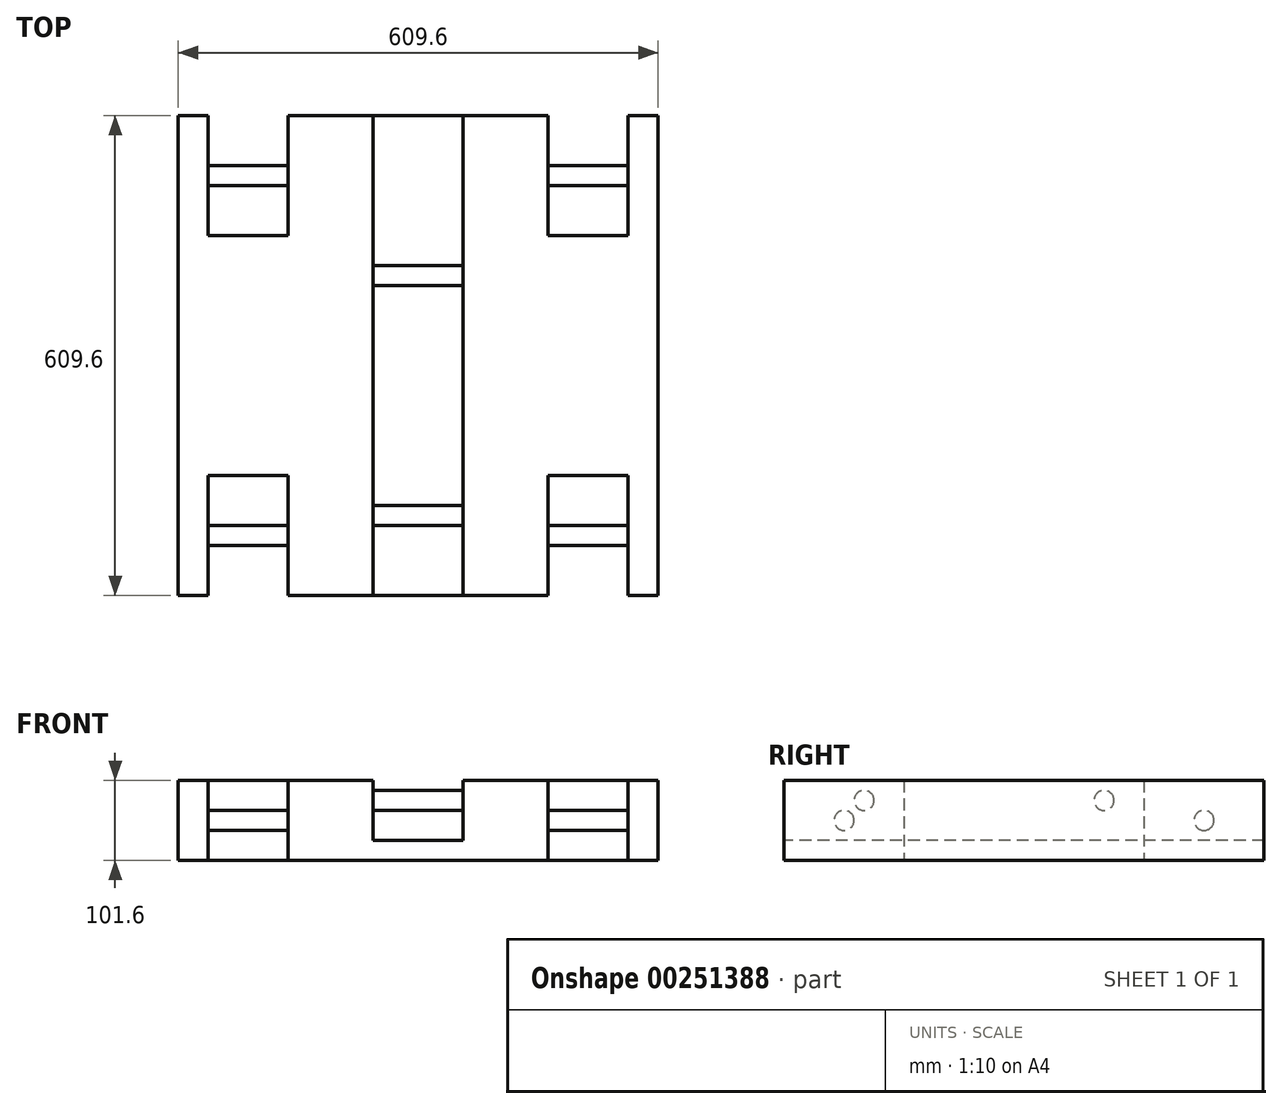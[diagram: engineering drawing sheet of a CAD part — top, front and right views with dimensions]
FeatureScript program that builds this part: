
annotation { "Feature Type Name" : "Feature", "Feature Type Description" : "" }
export const myFeature = defineFeature(function(context is Context, id is Id, definition is map)
    precondition{}
    {
        {
            var Q0;
            Q0=qCreatedBy(makeId("Top.planeOp"),FACE);
            var sketch = newSketch(context, id + "F0", { "sketchPlane" : qUnion([Q0])});
            skLineSegment(sketch, "E0.bottom", {"start": v(-126.74, -80.73) * mm, "end": v(482.86, -80.73) * mm});
            skLineSegment(sketch, "E0.top", {"start": v(-126.74, 528.87) * mm, "end": v(482.86, 528.87) * mm});
            skLineSegment(sketch, "E0.left", {"start": v(-126.74, -80.73) * mm, "end": v(-126.74, 528.87) * mm});
            skLineSegment(sketch, "E0.right", {"start": v(482.86, -80.73) * mm, "end": v(482.86, 528.87) * mm});
            skSolve(sketch);
        }
        {
            var Q0;
            Q0=makeQuery(id+"F0.imprint","IMPRINT",FACE,{"disambiguationData":[TD([[makeQuery(id+"F0.imprint","IMPRINT",EDGE,{"derivedFrom":sQuery(id+"F0.wireOp",EDGE,"E0.bottom")}),1.0]])]});
            extrude(context, id + "F1", {"entities" : qUnion([Q0]), "depth" : 101.6 * mm});
        }
        {
            var Q0;
            Q0=qCreatedBy(makeId("Top.planeOp"),FACE);
            var sketch = newSketch(context, id + "F2", { "sketchPlane" : qUnion([Q0])});
            skLineSegment(sketch, "E1.bottom", {"start": v(444.76, -80.73) * mm, "end": v(343.16, -80.73) * mm});
            skLineSegment(sketch, "E1.top", {"start": v(444.76, 71.67) * mm, "end": v(343.16, 71.67) * mm});
            skLineSegment(sketch, "E1.left", {"start": v(444.76, -80.73) * mm, "end": v(444.76, 71.67) * mm});
            skLineSegment(sketch, "E1.right", {"start": v(343.16, -80.73) * mm, "end": v(343.16, 71.67) * mm});
            skPoint(sketch, "E1.middle", {"position": v(393.96, 0) * mm});
            skLineSegment(sketch, "E2.bottom", {"start": v(12.96, -80.73) * mm, "end": v(-88.64, -80.73) * mm});
            skLineSegment(sketch, "E2.top", {"start": v(12.96, 71.67) * mm, "end": v(-88.64, 71.67) * mm});
            skLineSegment(sketch, "E2.left", {"start": v(12.96, -80.73) * mm, "end": v(12.96, 71.67) * mm});
            skLineSegment(sketch, "E2.right", {"start": v(-88.64, -80.73) * mm, "end": v(-88.64, 71.67) * mm});
            skPoint(sketch, "E2.middle", {"position": v(-37.84, -4.53) * mm});
            skLineSegment(sketch, "E3.bottom", {"start": v(-88.64, 528.87) * mm, "end": v(12.96, 528.87) * mm});
            skLineSegment(sketch, "E3.top", {"start": v(-88.64, 376.47) * mm, "end": v(12.96, 376.47) * mm});
            skLineSegment(sketch, "E3.left", {"start": v(-88.64, 528.87) * mm, "end": v(-88.64, 376.47) * mm});
            skLineSegment(sketch, "E3.right", {"start": v(12.96, 528.87) * mm, "end": v(12.96, 376.47) * mm});
            skLineSegment(sketch, "E4.bottom", {"start": v(444.76, 528.87) * mm, "end": v(343.16, 528.87) * mm});
            skLineSegment(sketch, "E4.top", {"start": v(444.76, 376.47) * mm, "end": v(343.16, 376.47) * mm});
            skLineSegment(sketch, "E4.left", {"start": v(444.76, 528.87) * mm, "end": v(444.76, 376.47) * mm});
            skLineSegment(sketch, "E4.right", {"start": v(343.16, 528.87) * mm, "end": v(343.16, 376.47) * mm});
            skSolve(sketch);
        }
        {
            var Q0;
            Q0 = qSketchRegion(id + "F2", true);
            extrude(context, id + "F3", {"entities" : qUnion([Q0]), "operationType" : NewBodyOperationType.REMOVE, "depth" : 101.6 * mm});
        }
        {
            var Q0;
            Q0=makeQuery(id+"F1.opExtrude","SWEPT_FACE",FACE,{"disambiguationData":[OSD([sQuery(id+"F0.wireOp",EDGE,"E0.left")])]});
            var sketch = newSketch(context, id + "F4", { "sketchPlane" : qUnion([Q0])});
            skCircle(sketch, "E5", {"center": v(-452.67, 50.8) * mm, "radius": 12.7 * mm});
            skCircle(sketch, "E6", {"center": v(4.53, 50.8) * mm, "radius": 12.7 * mm});
            skSolve(sketch);
        }
        {
            var Q0;
            Q0=makeQuery(id+"F4.imprint","IMPRINT",FACE,{"disambiguationData":[TD([[makeQuery(id+"F4.imprint","IMPRINT",EDGE,{"derivedFrom":sQuery(id+"F4.wireOp",EDGE,"E5")}),1.0]])]});
            var Q1;
            Q1=makeQuery(id+"F4.imprint","IMPRINT",FACE,{"disambiguationData":[TD([[makeQuery(id+"F4.imprint","IMPRINT",EDGE,{"derivedFrom":sQuery(id+"F4.wireOp",EDGE,"E6")}),1.0]])]});
            extrude(context, id + "F5", {"entities" : qUnion([Q0, Q1]), "operationType" : NewBodyOperationType.ADD, "oppositeDirection" : true, "depth" : 609.6 * mm});
        }
        {
            var Q0;
            Q0=makeQuery(id+"F1.opExtrude","CAP_FACE",FACE,{"disambiguationData":[OSD([sQuery(id+"F0.wireOp",EDGE,"E0.bottom"),sQuery(id+"F0.wireOp",EDGE,"E0.top"),sQuery(id+"F0.wireOp",EDGE,"E0.left"),sQuery(id+"F0.wireOp",EDGE,"E0.right")])],"isStart":false});
            var sketch = newSketch(context, id + "F6", { "sketchPlane" : qUnion([Q0])});
            skLineSegment(sketch, "E7.bottom", {"start": v(120.91, 528.87) * mm, "end": v(235.21, 528.87) * mm});
            skLineSegment(sketch, "E7.top", {"start": v(120.91, -80.73) * mm, "end": v(235.21, -80.73) * mm});
            skLineSegment(sketch, "E7.left", {"start": v(120.91, 528.87) * mm, "end": v(120.91, -80.73) * mm});
            skLineSegment(sketch, "E7.right", {"start": v(235.21, 528.87) * mm, "end": v(235.21, -80.73) * mm});
            skSolve(sketch);
        }
        {
            var Q0;
            Q0=makeQuery(id+"F6.imprint","IMPRINT",FACE,{"disambiguationData":[TD([[makeQuery(id+"F6.imprint","IMPRINT",EDGE,{"derivedFrom":sQuery(id+"F6.wireOp",EDGE,"E7.bottom")}),-1.0]])]});
            extrude(context, id + "F7", {"entities" : qUnion([Q0]), "operationType" : NewBodyOperationType.REMOVE, "oppositeDirection" : true, "depth" : 76.2 * mm});
        }
        {
            var Q0;
            Q0=makeQuery(id+"F7.boolean.opBoolean","COPY",FACE,{"derivedFrom":makeQuery(id+"F7.opExtrude","SWEPT_FACE",FACE,{"disambiguationData":[OSD([sQuery(id+"F6.wireOp",EDGE,"E7.left")])]})});
            var sketch = newSketch(context, id + "F8", { "sketchPlane" : qUnion([Q0])});
            skCircle(sketch, "E8", {"center": v(20.87, 76.2) * mm, "radius": 12.7 * mm});
            skCircle(sketch, "E9", {"center": v(325.67, 76.2) * mm, "radius": 12.7 * mm});
            skSolve(sketch);
        }
        {
            var Q0;
            Q0 = qSketchRegion(id + "F8", true);
            extrude(context, id + "F9", {"entities" : qUnion([Q0]), "operationType" : NewBodyOperationType.ADD, "endBound" : BoundingType.UP_TO_NEXT, "depth" : 25.4 * mm});
        }
    });
